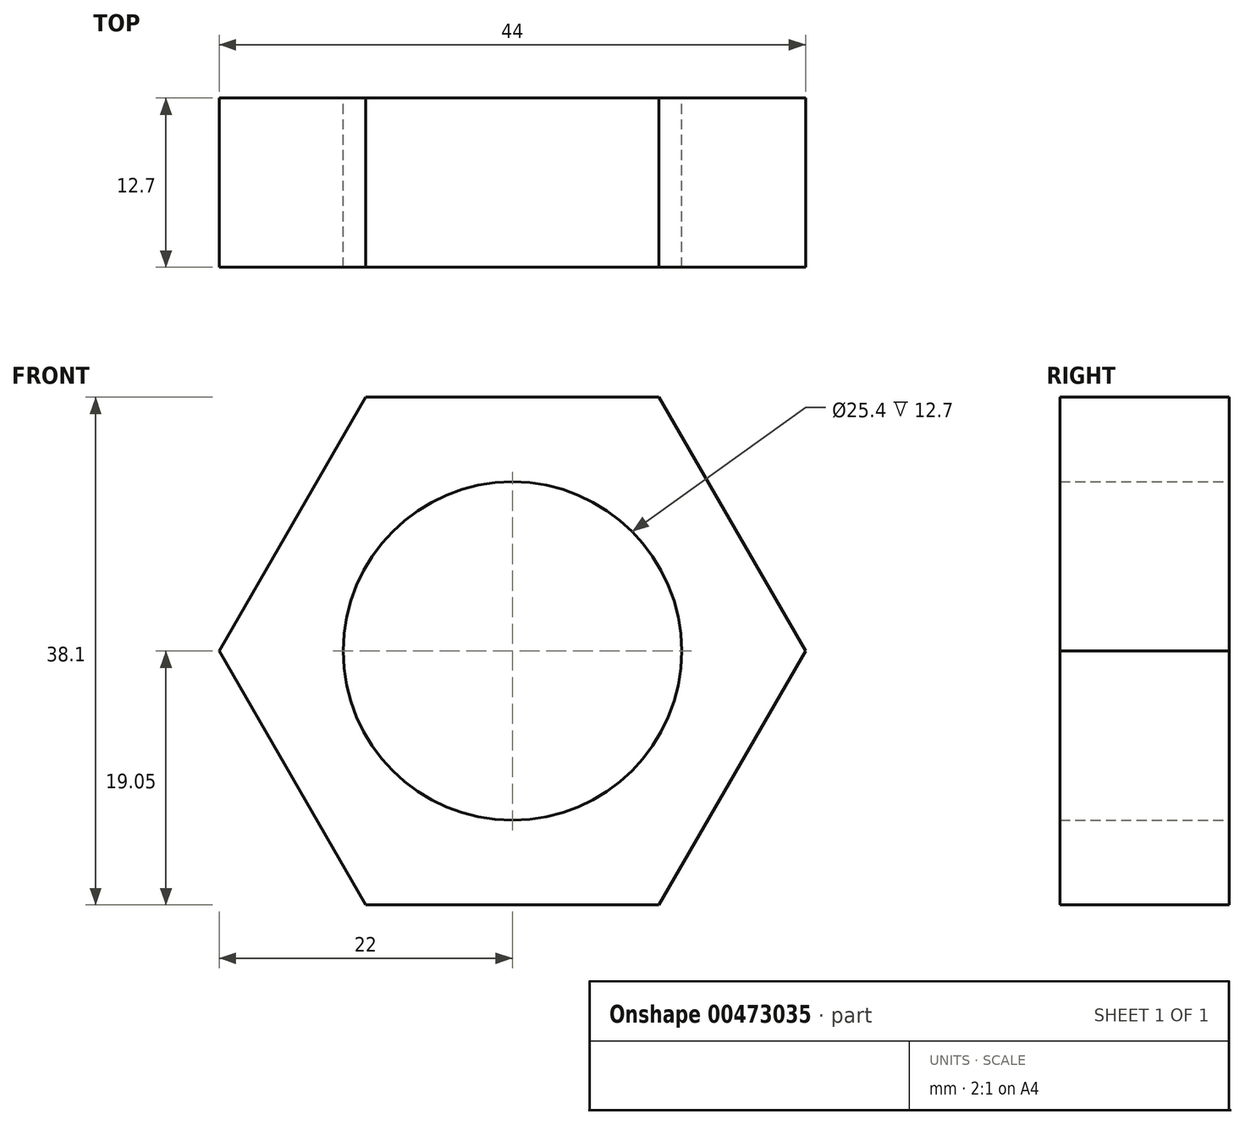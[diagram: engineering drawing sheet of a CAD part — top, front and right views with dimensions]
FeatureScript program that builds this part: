
annotation { "Feature Type Name" : "Feature", "Feature Type Description" : "" }
export const myFeature = defineFeature(function(context is Context, id is Id, definition is map)
    precondition{}
    {
        {
            var Q0;
            Q0=qCreatedBy(makeId("Front.planeOp"),FACE);
            var sketch = newSketch(context, id + "F0", { "sketchPlane" : qUnion([Q0])});
            skLineSegment(sketch, "E0", {"start": v(0, 0) * mm, "end": v(0, 19.05) * mm});
            skCircle(sketch, "E1", {"center": v(0, 0) * mm, "radius": 12.7 * mm});
            skCircle(sketch, "E2.cCircle", {"center": v(0, 0) * mm, "radius": 19.05 * mm, "construction": true});
            skLineSegment(sketch, "E2.0", {"start": v(-11, 19.05) * mm, "end": v(11, 19.05) * mm});
            skLineSegment(sketch, "E2.1", {"start": v(11, 19.05) * mm, "end": v(22, 0) * mm});
            skLineSegment(sketch, "E2.2", {"start": v(22, 0) * mm, "end": v(11, -19.05) * mm});
            skLineSegment(sketch, "E2.3", {"start": v(11, -19.05) * mm, "end": v(-11, -19.05) * mm});
            skLineSegment(sketch, "E2.4", {"start": v(-11, -19.05) * mm, "end": v(-22, 0) * mm});
            skLineSegment(sketch, "E2.5", {"start": v(-22, 0) * mm, "end": v(-11, 19.05) * mm});
            skPoint(sketch, "E2.0.midPoint", {"position": v(0, 19.05) * mm});
            skSolve(sketch);
        }
        {
            var Q0;
            Q0=makeQuery(id+"F0.imprint","IMPRINT",FACE,{"disambiguationData":[TD([[makeQuery(id+"F0.imprint","IMPRINT",EDGE,{"derivedFrom":sQuery(id+"F0.wireOp",EDGE,"E1")}),-1.0]])]});
            extrude(context, id + "F1", {"entities" : qUnion([Q0]), "depth" : 12.7 * mm});
        }
    });
